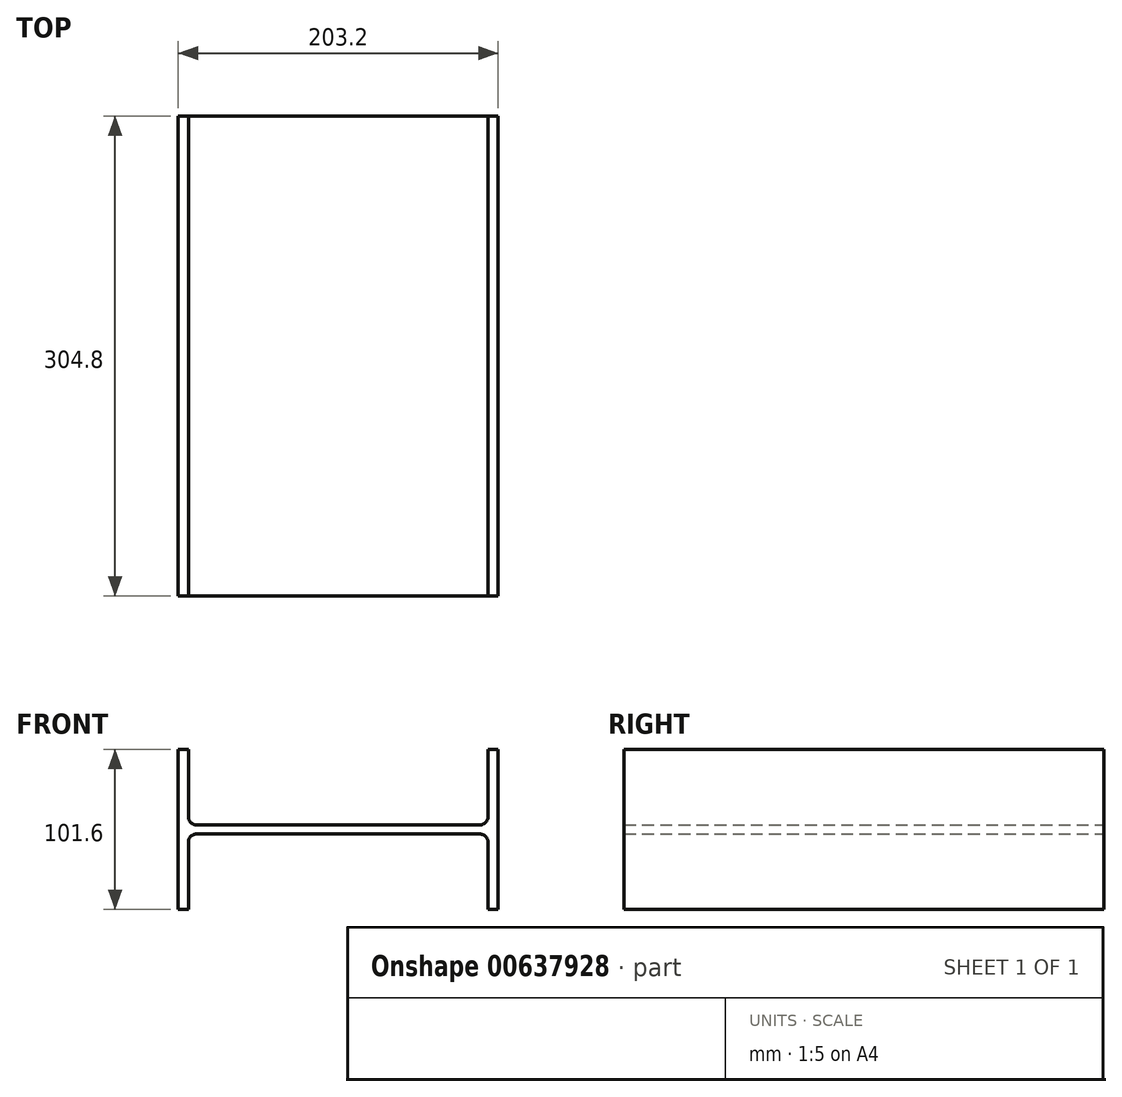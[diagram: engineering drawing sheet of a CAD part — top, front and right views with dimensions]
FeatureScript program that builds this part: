
annotation { "Feature Type Name" : "Feature", "Feature Type Description" : "" }
export const myFeature = defineFeature(function(context is Context, id is Id, definition is map)
    precondition{}
    {
        {
            var Q0;
            Q0=qCreatedBy(makeId("Front.planeOp"),FACE);
            var sketch = newSketch(context, id + "F0", { "sketchPlane" : qUnion([Q0])});
            skLineSegment(sketch, "E0.bottom", {"start": v(101.6, -50.8) * mm, "end": v(95.12, -50.8) * mm});
            skLineSegment(sketch, "E0.top", {"start": v(101.6, 50.8) * mm, "end": v(95.12, 50.8) * mm});
            skLineSegment(sketch, "E0.left", {"start": v(101.6, -50.8) * mm, "end": v(101.6, 50.8) * mm});
            skLineSegment(sketch, "E0.right", {"start": v(-101.6, -50.8) * mm, "end": v(-101.6, 50.8) * mm});
            skPoint(sketch, "E0.middle", {"position": v(0, 0) * mm});
            skLineSegment(sketch, "E1.0", {"start": v(-95.12, -50.8) * mm, "end": v(-95.12, -2.92) * mm});
            skLineSegment(sketch, "E2.0", {"start": v(95.12, -50.8) * mm, "end": v(95.12, -2.92) * mm});
            skLineSegment(sketch, "E3", {"start": v(-95.12, 2.92) * mm, "end": v(95.12, 2.92) * mm});
            skLineSegment(sketch, "E4.MirrorCS", {"start": v(-95.12, -2.92) * mm, "end": v(95.12, -2.92) * mm});
            skLineSegment(sketch, "E5.trimOffspring", {"start": v(-95.12, 50.8) * mm, "end": v(-101.6, 50.8) * mm});
            skLineSegment(sketch, "E6.trimOffspring", {"start": v(-95.12, -50.8) * mm, "end": v(-101.6, -50.8) * mm});
            skLineSegment(sketch, "E7.trimOffspring", {"start": v(-95.12, 2.92) * mm, "end": v(-95.12, 50.8) * mm});
            skLineSegment(sketch, "E8.trimOffspring", {"start": v(95.12, 2.92) * mm, "end": v(95.12, 50.8) * mm});
            skSolve(sketch);
        }
        {
            var Q0;
            Q0 = qSketchRegion(id + "F0", true);
            extrude(context, id + "F1", {"entities" : qUnion([Q0]), "endBound" : BoundingType.SYMMETRIC, "depth" : 304.8 * mm, "offsetDistance" : 25.4 * mm});
        }
        {
            var Q0;
            Q0=makeQuery(id+"F1.opExtrude","SWEPT_EDGE",EDGE,{"disambiguationData":[OSD([sQuery(id+"F0.wireOp",EDGE,"E3"),sQuery(id+"F0.wireOp",EDGE,"E7.trimOffspring")])]});
            var Q1;
            Q1=makeQuery(id+"F1.opExtrude","SWEPT_EDGE",EDGE,{"disambiguationData":[OSD([sQuery(id+"F0.wireOp",EDGE,"E1.0"),sQuery(id+"F0.wireOp",EDGE,"E4.MirrorCS")])]});
            var Q2;
            Q2=makeQuery(id+"F1.opExtrude","SWEPT_EDGE",EDGE,{"disambiguationData":[OSD([sQuery(id+"F0.wireOp",EDGE,"E2.0"),sQuery(id+"F0.wireOp",EDGE,"E4.MirrorCS")])]});
            var Q3;
            Q3=makeQuery(id+"F1.opExtrude","SWEPT_EDGE",EDGE,{"disambiguationData":[OSD([sQuery(id+"F0.wireOp",EDGE,"E3"),sQuery(id+"F0.wireOp",EDGE,"E8.trimOffspring")])]});
            fillet(context, id + "F2", {"entities" : qUnion([Q0, Q1, Q2, Q3]), "radius" : 5.08 * mm, "tangentPropagation" : true, "allowEdgeOverflow" : false});
        }
    });
